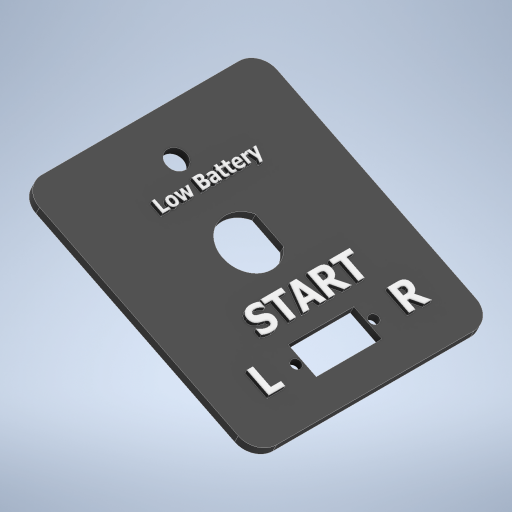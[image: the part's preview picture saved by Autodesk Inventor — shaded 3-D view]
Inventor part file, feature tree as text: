
AUTODESK INVENTOR PART (.ipt)
format: ipt  version: 2024.2 (Build 282272000, 272)  size: 866,816 bytes
history: native  units: mm
features: sketch x10, extrude x9, projected_geometry x4, fillet x2, emboss x1
ambient origin geometry x8: Origin, YZ Plane, XZ Plane, XY Plane, X Axis, Y Axis, Z Axis, Center Point
bodies: Solid1 (feature_tree)
feature tree (26):
  extrude  "Extrusion1"  Depth=2.0mm
  extrude  "Extrusion2"  Depth=6.5mm
  extrude  "Extrusion3"  Depth=9.0mm TaperAngle=0.0deg
  extrude  "Extrusion5"  Depth=9.0mm TaperAngle=0.0deg
  emboss  "Emboss1"
  extrude  "Extrusion6"  Depth=20.0mm
  extrude  "Extrusion7"  Depth=5.0mm
  extrude  "Extrusion8"  Depth=16.3mm
  extrude  "Extrusion9"  Depth=10.0mm
  fillet  "Fillet1"  Radius=20.0mm
  extrude  "Extrusion10"  Depth=8.15mm
  fillet  "Fillet2"  Radius=20.0mm
  sketch  "Sketch2"  dims[d4=2.0mm d5=2.0mm]
  sketch  "Sketch3"  dims[d6=38.25mm d8=6.5mm]
  projected_geometry  "Projected Loop1"
  sketch  "Sketch4"  dims[d9=8.0mm d10=9.0mm d11=0.0mm]
  projected_geometry  "Projected Loop2"
  projected_geometry  "Projected Loop3"
  projected_geometry  "Projected Loop4"
  sketch  "Sketch7"  dims[d12=41.0mm d13=0.0mm d14=9.0mm d15=0.0mm]
  sketch  "Sketch8"  dims[d16=15.0mm d29=20.0mm]
  sketch  "Sketch9"  dims[d30=5.0mm d31=13.0mm]
  sketch  "Sketch10"  dims[d32=29.5mm d33=16.3mm]
  sketch  "Sketch11"  dims[d34=5.2mm d35=10.0mm d36=20.0mm]
  sketch  "Sketch12"  dims[d37=7.8mm d38=8.15mm d39=20.0mm]
  sketch  "Sketch13"  dims[d40=0.0mm d41=0.0mm d42=1.0mm d43=0.0mm d44=49.0mm d45=3.0mm d46=3.0mm d47=3.25mm d48=3.25mm d49=4.0mm d50=2.5mm d51=0.0mm d52=3.0mm d53=3.0mm d54=51.0mm d55=4.0mm d56=4.0mm d57=2.5mm d58=0.0mm d59=135.0deg d60=20.0mm d61=135.0deg d62=20.0mm d63=65.018mm d64=0.0mm d65=0.0mm d66=0.0mm d67=2.3mm d68=2.3mm d69=1.5mm d70=1.5mm d71=3.9mm d72=3.9mm d73=5.0mm d74=4.0mm d75=4.0mm d76=47.0mm d78=48.0mm d79=46.0mm d81=1.0mm d82=12.0mm d83=1.58mm d84=1.5mm d85=0.0mm d86=2.0mm]
